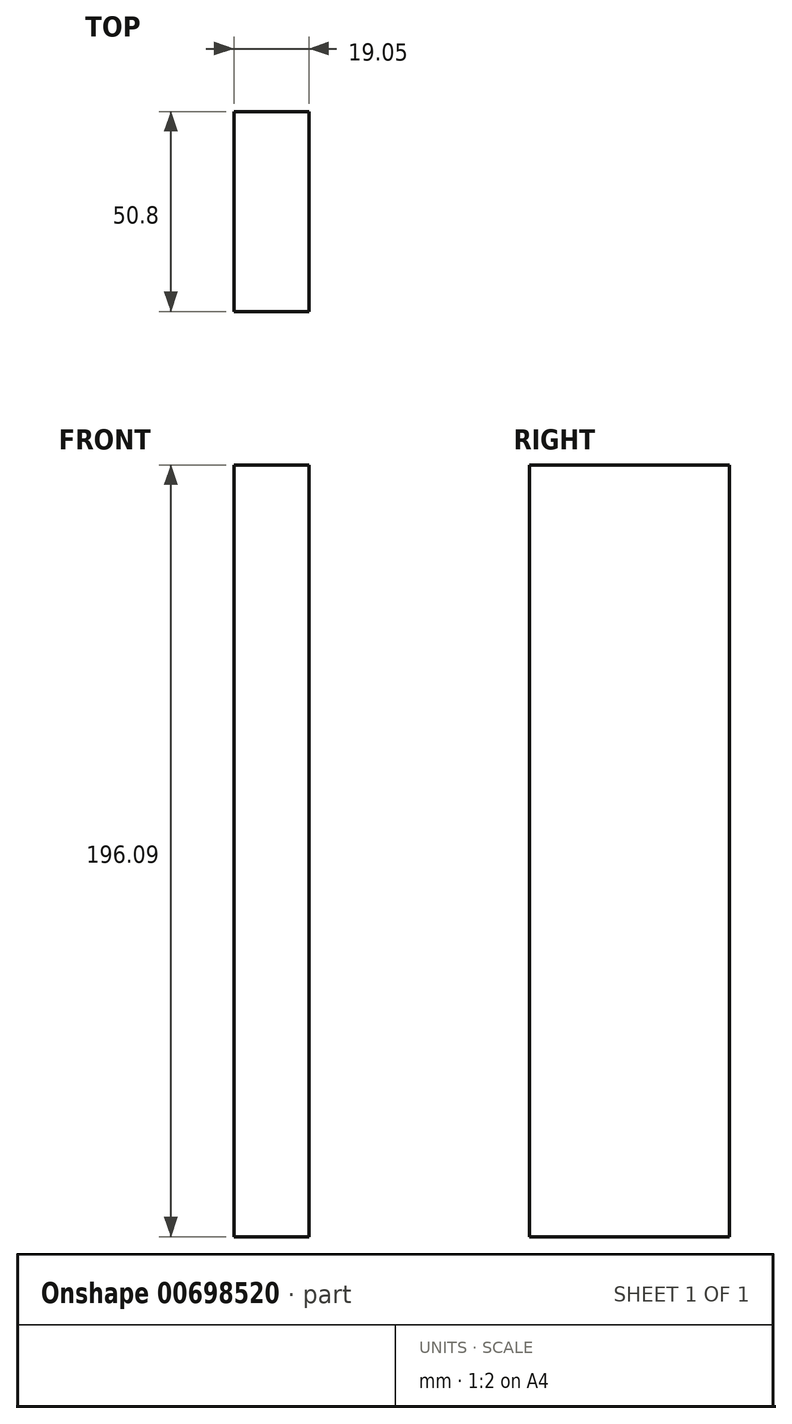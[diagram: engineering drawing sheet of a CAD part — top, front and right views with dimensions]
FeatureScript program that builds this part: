
annotation { "Feature Type Name" : "Feature", "Feature Type Description" : "" }
export const myFeature = defineFeature(function(context is Context, id is Id, definition is map)
    precondition{}
    {
        {
            var Q0;
            Q0=qCreatedBy(makeId("Right.planeOp"),FACE);
            var sketch = newSketch(context, id + "F0", { "sketchPlane" : qUnion([Q0])});
            skLineSegment(sketch, "E0.bottom", {"start": v(-72.37, -121.98) * mm, "end": v(-21.57, -121.98) * mm});
            skLineSegment(sketch, "E0.top", {"start": v(-72.37, 74.1) * mm, "end": v(-21.57, 74.1) * mm});
            skLineSegment(sketch, "E0.left", {"start": v(-72.37, -121.98) * mm, "end": v(-72.37, 74.1) * mm});
            skLineSegment(sketch, "E0.right", {"start": v(-21.57, -121.98) * mm, "end": v(-21.57, 74.1) * mm});
            skSolve(sketch);
        }
        {
            var Q0;
            Q0 = qSketchRegion(id + "F0", true);
            extrude(context, id + "F1", {"entities" : qUnion([Q0]), "depth" : 19.05 * mm, "offsetDistance" : 25.4 * mm});
        }
    });
